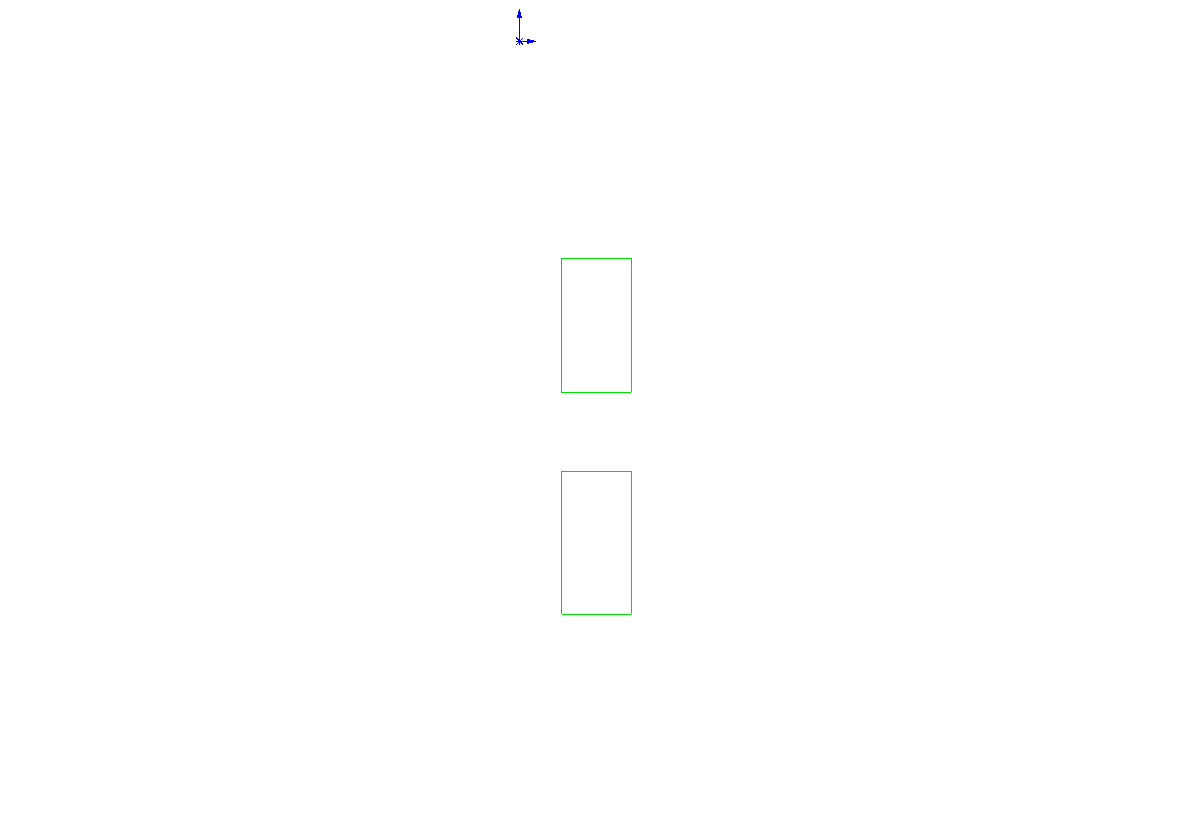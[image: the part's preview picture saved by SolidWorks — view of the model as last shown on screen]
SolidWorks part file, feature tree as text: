
SOLIDWORKS PART (.sldprt)
format: sldprt  version: not decoded by parser v0  size: 224,256 bytes
history: native  units: mm
features: sketch x4, cut_extrude x3, material x1, extrude x1 (+13 scaffold rows collapsed)
feature tree (22):
  scaffold x13  (default folders/planes/origin — collapsed)
  material  "Material <not specified>"
  sketch  "Sketch1"  dims[D1=18.542mm D2=95.25mm]
  extrude  "Extrude1"  Depth=1.6002mm
  sketch  "Sketch2"  dims[D1=3.6068mm D2=3.5052mm D3=9.525mm D4=6.35mm D5=9.525mm D6=6.35mm]
  cut_extrude  "Cut-Extrude1"  Depth=1.6002mm
  sketch  "Sketch3"  dims[D1=3.556mm D2=4.7498mm D3=11.43mm D4=5.6388mm D5=63.5mm]
  cut_extrude  "Cut-Extrude2"  Depth=2.54mm
  sketch  "Sketch4"  dims[c1.D3=3.556mm c1.D2=3.556mm c1.D7=3.556mm c1.D1=20.32mm c2.D2=8.89mm c2.D3=9.525mm c2.D4=3.175mm c2.D5=20.32mm c2.D6=9.525mm c2.D7=8.89mm c2.D8=3.175mm]
  cut_extrude  "Fiber Holes"  Depth=2.54mm
decode coverage: 8 of 8 modeling features carry decoded parameters
note: suppression state not decoded; provenance and decode notes live in map.json
